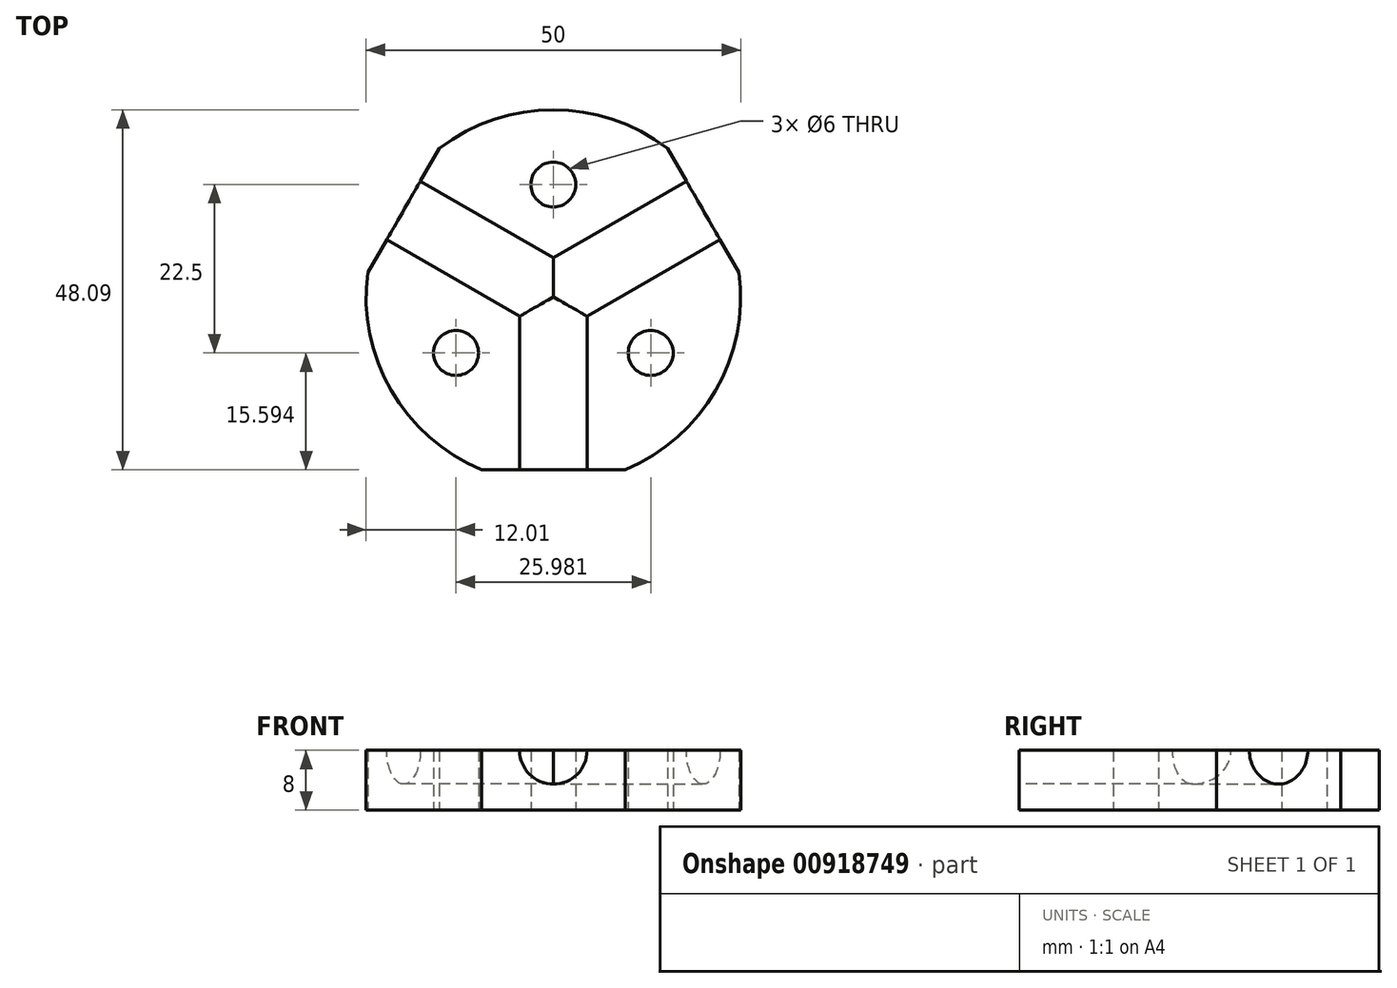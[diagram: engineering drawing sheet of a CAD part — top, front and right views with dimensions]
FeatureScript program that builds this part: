
annotation { "Feature Type Name" : "Feature", "Feature Type Description" : "" }
export const myFeature = defineFeature(function(context is Context, id is Id, definition is map)
    precondition{}
    {
        {
            var Q0;
            Q0=qCreatedBy(makeId("Top.planeOp"),FACE);
            var sketch = newSketch(context, id + "F0", { "sketchPlane" : qUnion([Q0])});
            skLineSegment(sketch, "E0", {"start": v(15.21, 26.35) * mm, "end": v(24.79, 42.93) * mm});
            skLineSegment(sketch, "E1", {"start": v(55.21, 42.93) * mm, "end": v(64.79, 26.35) * mm});
            skLineSegment(sketch, "E2", {"start": v(30.43, 0) * mm, "end": v(49.57, 0) * mm});
            skPoint(sketch, "E3.orphan", {"position": v(80, 0) * mm});
            skLineSegment(sketch, "E4", {"start": v(20, 34.64) * mm, "end": v(40, 23.1) * mm, "construction": true});
            skLineSegment(sketch, "E5", {"start": v(60, 34.64) * mm, "end": v(40, 23.1) * mm, "construction": true});
            skLineSegment(sketch, "E6", {"start": v(40, 0) * mm, "end": v(40, 23.1) * mm, "construction": true});
            skArc(sketch, "E7", {"start": v(55.21, 42.93) * mm, "mid": v(40, 48.1) * mm, "end": v(24.79, 42.93) * mm});
            skPoint(sketch, "E8.orphan", {"position": v(40, 69.28) * mm});
            skArc(sketch, "E9.trimOffspring", {"start": v(15.21, 26.35) * mm, "mid": v(18.35, 10.6) * mm, "end": v(30.43, 0) * mm});
            skPoint(sketch, "E10.orphan", {"position": v(0, 0) * mm});
            skArc(sketch, "E11.trimOffspring", {"start": v(49.57, 0) * mm, "mid": v(61.65, 10.6) * mm, "end": v(64.79, 26.35) * mm});
            skLineSegment(sketch, "E12", {"start": v(40, 23.1) * mm, "end": v(61.65, 10.6) * mm, "construction": true});
            skLineSegment(sketch, "E13", {"start": v(40, 48.1) * mm, "end": v(40, 23.1) * mm, "construction": true});
            skLineSegment(sketch, "E14", {"start": v(40, 23.1) * mm, "end": v(18.35, 10.6) * mm, "construction": true});
            skCircle(sketch, "E15", {"center": v(40, 38.1) * mm, "radius": 3 * mm});
            skCircle(sketch, "E16", {"center": v(27, 15.6) * mm, "radius": 3 * mm});
            skCircle(sketch, "E17", {"center": v(53, 15.6) * mm, "radius": 3 * mm});
            skSolve(sketch);
        }
        {
            var Q0;
            Q0 = qSketchRegion(id + "F0", true);
            extrude(context, id + "F1", {"entities" : qUnion([Q0]), "depth" : 8 * mm, "offsetDistance" : 25 * mm});
        }
        {
            var Q0;
            Q0=makeQuery(id+"F1.opExtrude","SWEPT_FACE",FACE,{"disambiguationData":[OSD([sQuery(id+"F0.wireOp",EDGE,"E2")])]});
            var sketch = newSketch(context, id + "F2", { "sketchPlane" : qUnion([Q0])});
            skCircle(sketch, "E18", {"center": v(40, 8) * mm, "radius": 4.5 * mm});
            skSolve(sketch);
        }
        {
            var Q0;
            Q0 = qSketchRegion(id + "F2", true);
            extrude(context, id + "F3", {"entities" : qUnion([Q0]), "operationType" : NewBodyOperationType.REMOVE, "oppositeDirection" : true, "depth" : 23.2 * mm, "offsetDistance" : 25 * mm});
        }
        {
            var Q0;
            Q0=makeQuery(id+"F1.opExtrude","SWEPT_FACE",FACE,{"disambiguationData":[OSD([sQuery(id+"F0.wireOp",EDGE,"E1")])]});
            var sketch = newSketch(context, id + "F4", { "sketchPlane" : qUnion([Q0])});
            skCircle(sketch, "E19", {"center": v(0, 8) * mm, "radius": 4.5 * mm});
            skSolve(sketch);
        }
        {
            var Q0;
            Q0 = qSketchRegion(id + "F4", true);
            extrude(context, id + "F5", {"entities" : qUnion([Q0]), "operationType" : NewBodyOperationType.REMOVE, "oppositeDirection" : true, "depth" : 23.2 * mm, "offsetDistance" : 25 * mm});
        }
        {
            var Q0;
            Q0=makeQuery(id+"F1.opExtrude","SWEPT_FACE",FACE,{"disambiguationData":[OSD([sQuery(id+"F0.wireOp",EDGE,"E0")])]});
            var sketch = newSketch(context, id + "F6", { "sketchPlane" : qUnion([Q0])});
            skCircle(sketch, "E20", {"center": v(-40, 8) * mm, "radius": 4.5 * mm});
            skSolve(sketch);
        }
        {
            var Q0;
            Q0 = qSketchRegion(id + "F6", true);
            extrude(context, id + "F7", {"entities" : qUnion([Q0]), "operationType" : NewBodyOperationType.REMOVE, "oppositeDirection" : true, "depth" : 23.2 * mm, "offsetDistance" : 25 * mm});
        }
    });
